# Revit family: Ventüer_VentilationLouvres_VL-55S
name_source: partatom
category: Generic Models
units: mm (PartAtom-declared; Revit-internal decimal feet)

## family parameters
Always vertical = No
Can host rebar = No
Cut with Voids When Loaded = Yes
Part Type = Normal
Room Calculation Point = No
Round Connector Dimension = Use Diameter
Shared = No
Work Plane-Based = Yes

## types (3) — shared parameters
Aerodynamic Performance = Air Inlet: 0.226, Class 3. Air Extract: 0.231, Class 3
Ancillaries = Bird Mesh, Insect Mesh, Solid Blanking, Perimeter Mounting Angle
Blade Centres = 55 mm  [stored 0.180446 ft]
Blade Count = 9
Blade Cut Offset = 495 mm  [stored 1.62402 ft]
Blade Material = Ventüer Aluminium
Default Elevation = 1219 mm
Description = Slimline Ventilation and Screening
Exact Neck Height = 594 mm  [stored 1.94882 ft]
Exact Neck Height Check = 594 mm  [stored 1.94882 ft]
Exact Neck Width = 594 mm  [stored 1.94882 ft]
Exact Neck Width Check = 594 mm  [stored 1.94882 ft]
Flatbar = Yes
Frame Material = Ventüer Aluminium
Frame Set Count = 1
Frame Set Count Check = 2
Frame Set Transition Count = 1
Frame Set Transition Count Check = 2
Manufacturer = Ventüer
Max Flow = 5000.0 L/s
Min Flow = 100.0 L/s
Model = VL-55S
Multiple Frame Set = No
Multiple Transition = No
Noise Level NC Max = 0.00 NC
Noise Level NC Min = 0.00 NC
Nominal Height = 600 mm
Nominal Width = 600 mm
Nominated Air Flow = 100.0 L/s
Nominated Pessure Drop = 21.0 Pa
Rain Defence Performance = Class C - up to 1.0m/s suction velocity. Class D - up to 3.5m/s suction velocity
Single Frame Set = Yes
Single Transition = No
Specified Air Flow = 0.0 L/s
Specified Pressure Drop = 21.0 Pa
Static Pressure Max = 60.0 Pa
Static Pressure Min = 10.0 Pa
Tee = No
URL = https://www.ventuer.co
Ventüer Product Range = Ventilation Louvres

## per-type parameters (varying)
| type | Base Width | Blade And Frame Gap | Blade Offset | Channel | Connector Height | Connector Width | Depth | Flanged | Frame Set Width | Glazed | Overall Opening Height | Overall Opening Width | Profile Width | Screen Symbol Distance | Single Frame Set Width | Top Blade Height |
| VL-55S_CF | 3 mm  [stored 0.00984252 ft] | 28 mm  [stored 0.0918635 ft] | 6 mm  [stored 0.019685 ft] | Yes | 588 mm | 588 mm | 50 mm  [stored 0.164042 ft] | No | 588 mm | No | 588 mm | 588 mm | 3 mm  [stored 0.00984252 ft] | 3 mm  [stored 0.00984252 ft] | 294 mm | 65 mm |
| VL-55S_GF | 26 mm | 6 mm  [stored 0.019685 ft] | 9 mm  [stored 0.0295276 ft] | No | 542 mm  [stored 1.77822 ft] | 542 mm  [stored 1.77822 ft] | 50 mm  [stored 0.164042 ft] | No | 542 mm  [stored 1.77822 ft] | Yes | 542 mm  [stored 1.77822 ft] | 542 mm  [stored 1.77822 ft] | 26 mm | 6 mm  [stored 0.019685 ft] | 271 mm  [stored 0.889108 ft] | 41 mm |
| VL-55S_FF | 24 mm  [stored 0.0787402 ft] | 6 mm  [stored 0.019685 ft] | 4 mm  [stored 0.0131234 ft] | No | 546 mm  [stored 1.79134 ft] | 546 mm  [stored 1.79134 ft] | 45 mm  [stored 0.147638 ft] | Yes | 546 mm  [stored 1.79134 ft] | No | 546 mm  [stored 1.79134 ft] | 546 mm  [stored 1.79134 ft] | 24 mm  [stored 0.0787402 ft] | 2 mm  [stored 0.00656168 ft] | 273 mm  [stored 0.895669 ft] | 45 mm  [stored 0.147638 ft] |

note: column(s) folded — value = type name in every type: Keynote

note: [stored X ft] marks values corroborated as IEEE doubles in the binary element streams (Revit-internal decimal feet)

## geometry (parser evidence)
native form markers: Sweep x14
no freeform markers — native parametric forms only
